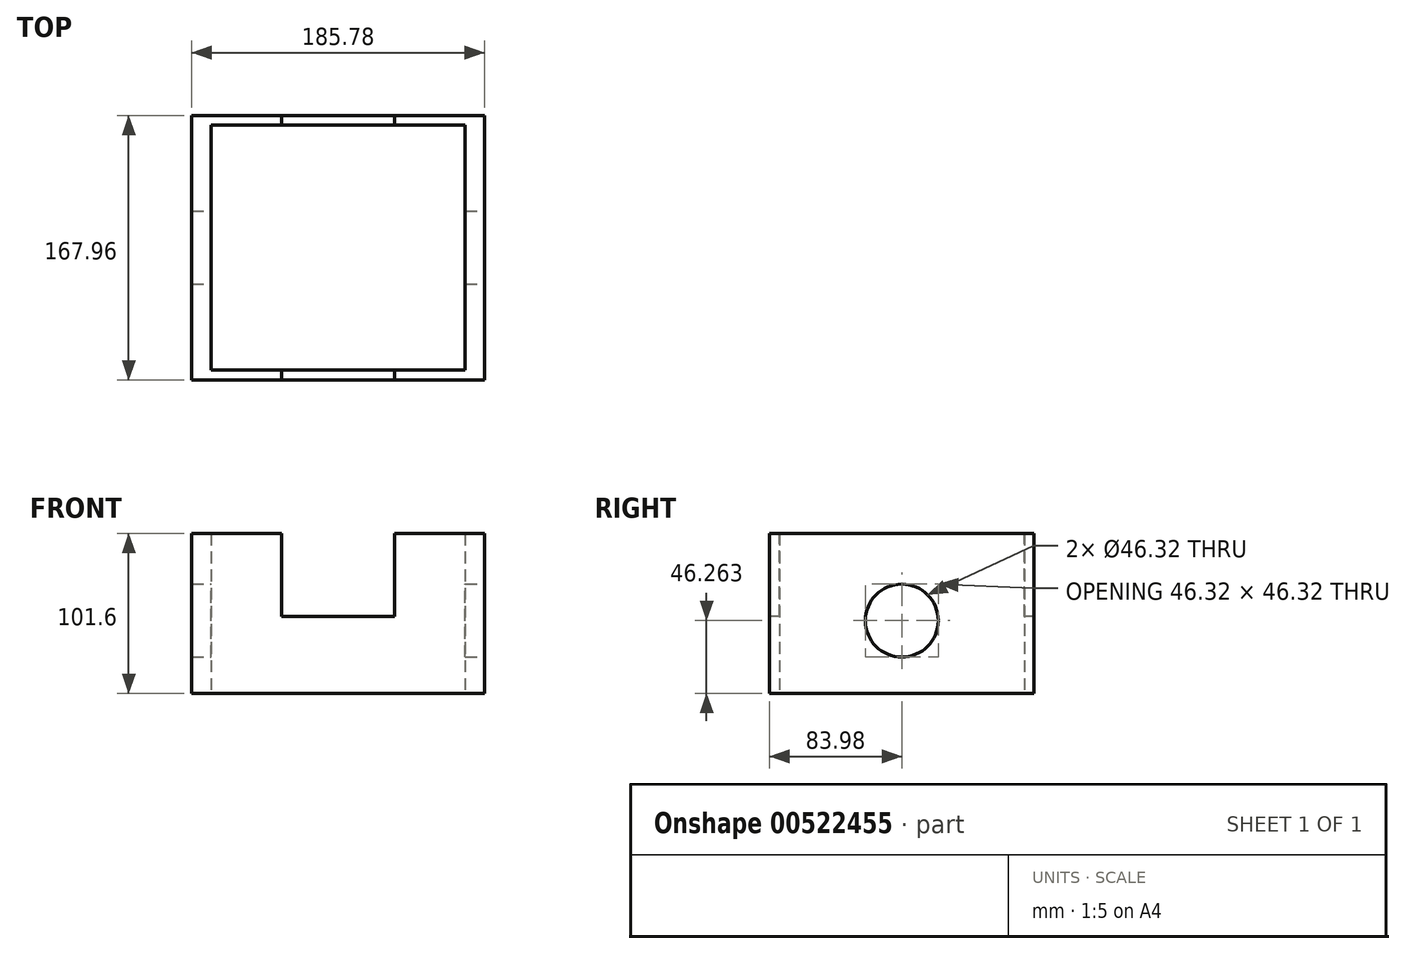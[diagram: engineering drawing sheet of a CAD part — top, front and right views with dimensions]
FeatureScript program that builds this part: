
annotation { "Feature Type Name" : "Feature", "Feature Type Description" : "" }
export const myFeature = defineFeature(function(context is Context, id is Id, definition is map)
    precondition{}
    {
        {
            var Q0;
            Q0=qCreatedBy(makeId("Top.planeOp"),FACE);
            var sketch = newSketch(context, id + "F0", { "sketchPlane" : qUnion([Q0])});
            skLineSegment(sketch, "E0.bottom", {"start": v(92.9, -83.98) * mm, "end": v(-92.9, -83.98) * mm});
            skLineSegment(sketch, "E0.top", {"start": v(92.9, 83.98) * mm, "end": v(-92.9, 83.98) * mm});
            skLineSegment(sketch, "E0.left", {"start": v(92.9, -83.98) * mm, "end": v(92.9, 83.98) * mm});
            skLineSegment(sketch, "E0.right", {"start": v(-92.9, -83.98) * mm, "end": v(-92.9, 83.98) * mm});
            skPoint(sketch, "E0.middle", {"position": v(0, 0) * mm});
            skSolve(sketch);
        }
        {
            var Q0;
            Q0 = qSketchRegion(id + "F0", true);
            extrude(context, id + "F1", {"entities" : qUnion([Q0]), "depth" : 101.6 * mm, "offsetDistance" : 25.4 * mm});
        }
        {
            var Q0;
            Q0=qCreatedBy(makeId("Front.planeOp"),FACE);
            var sketch = newSketch(context, id + "F2", { "sketchPlane" : qUnion([Q0])});
            skLineSegment(sketch, "E1.bottom", {"start": v(-35.8, 104.52) * mm, "end": v(35.8, 104.52) * mm});
            skLineSegment(sketch, "E1.top", {"start": v(-35.8, 48.93) * mm, "end": v(35.8, 48.93) * mm});
            skLineSegment(sketch, "E1.left", {"start": v(-35.8, 104.52) * mm, "end": v(-35.8, 48.93) * mm});
            skLineSegment(sketch, "E1.right", {"start": v(35.8, 104.52) * mm, "end": v(35.8, 48.93) * mm});
            skPoint(sketch, "E1.middle", {"position": v(0, 76.72) * mm});
            skSolve(sketch);
        }
        {
            var Q0;
            Q0 = qSketchRegion(id + "F2", true);
            extrude(context, id + "F3", {"entities" : qUnion([Q0]), "operationType" : NewBodyOperationType.REMOVE, "endBound" : BoundingType.SYMMETRIC, "oppositeDirection" : true, "depth" : 1270 * mm, "offsetDistance" : 25.4 * mm});
        }
        {
            var Q0;
            Q0=makeQuery(id+"F1.opExtrude","CAP_FACE",FACE,{"disambiguationData":[OSD([sQuery(id+"F0.wireOp",EDGE,"E0.bottom"),sQuery(id+"F0.wireOp",EDGE,"E0.top"),sQuery(id+"F0.wireOp",EDGE,"E0.left"),sQuery(id+"F0.wireOp",EDGE,"E0.right")])],"isStart":true});
            var sketch = newSketch(context, id + "F4", { "sketchPlane" : qUnion([Q0])});
            skLineSegment(sketch, "E2.bottom", {"start": v(80.7, -77.82) * mm, "end": v(-80.7, -77.82) * mm});
            skLineSegment(sketch, "E2.top", {"start": v(80.7, 77.82) * mm, "end": v(-80.7, 77.82) * mm});
            skLineSegment(sketch, "E2.left", {"start": v(80.7, -77.82) * mm, "end": v(80.7, 77.82) * mm});
            skLineSegment(sketch, "E2.right", {"start": v(-80.7, -77.82) * mm, "end": v(-80.7, 77.82) * mm});
            skPoint(sketch, "E2.middle", {"position": v(0, 0) * mm});
            skSolve(sketch);
        }
        {
            var Q0;
            Q0 = qSketchRegion(id + "F4", true);
            extrude(context, id + "F5", {"entities" : qUnion([Q0]), "operationType" : NewBodyOperationType.REMOVE, "oppositeDirection" : true, "depth" : 1270 * mm, "offsetDistance" : 25.4 * mm});
        }
        {
            var Q0;
            Q0=qCreatedBy(makeId("Right.planeOp"),FACE);
            var sketch = newSketch(context, id + "F6", { "sketchPlane" : qUnion([Q0])});
            skCircle(sketch, "E3", {"center": v(0, 46.26) * mm, "radius": 23.16 * mm});
            skSolve(sketch);
        }
        {
            var Q0;
            Q0 = qSketchRegion(id + "F6", true);
            extrude(context, id + "F7", {"entities" : qUnion([Q0]), "operationType" : NewBodyOperationType.REMOVE, "endBound" : BoundingType.SYMMETRIC, "oppositeDirection" : true, "depth" : 1270 * mm, "offsetDistance" : 25.4 * mm});
        }
    });
